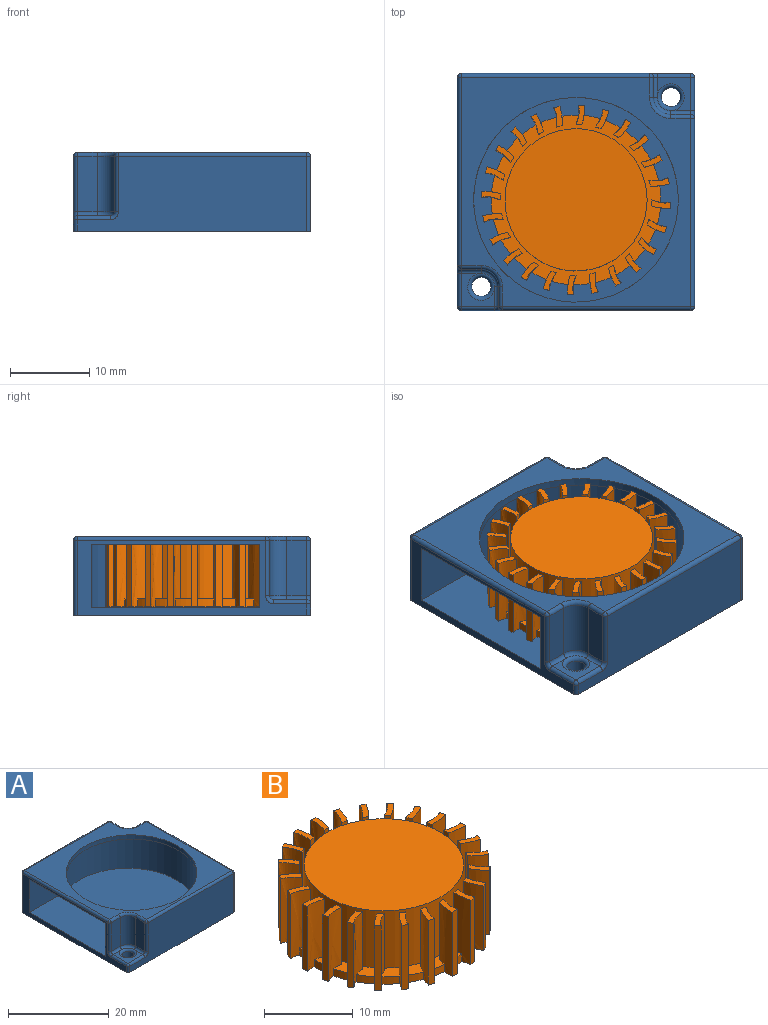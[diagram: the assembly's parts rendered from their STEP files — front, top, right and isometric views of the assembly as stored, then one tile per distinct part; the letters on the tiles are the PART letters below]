
ASSEMBLY  parts=2 mates=1
PART A: 64 faces, bbox 30x30x10 mm
  f0: plane 29x9.5mm, normal (-1,0,0), area 63.7mm2, adj f7,f21,f29,f32,f36,f45,f46,f58
  f1: plane 29x9.5mm, normal (0,1,0), area 234.1mm2, adj f7,f40,f46,f51,f54,f55,f57
  f2: plane 29x9.5mm, normal (1,0,0), area 234.1mm2, adj f7,f25,f33,f34,f37,f40,f41
  f3: plane 29x29mm, normal (0,0,1), area 263.2mm2, adj f26,f27,f31,f34,f35,f44,f45,f49
  f4: cylinder r=1.2mm len=2.4mm, axis (0,0,-1), area 11.3mm2, adj f7,f42
  f5: plane 29x9.5mm, normal (0,-1,0), area 234.1mm2, adj f7,f16,f17,f20,f21,f25,f26
  f6: cylinder r=1.2mm len=2.4mm, axis (0,0,-1), area 11.3mm2, adj f7,f19
  f7: plane 30x30mm, normal (0,0,-1), area 890.7mm2, adj f0,f1,f2,f4,f5,f6,f21,f25
  f8: plane 7x2.5mm, normal (-1,0,0), area 17.5mm2, adj f9,f17,f18,f27
  f9: cylinder r=2.2mm len=7mm, axis (0,0,1), area 24.2mm2, adj f8,f10,f23,f31
  f10: plane 7x2.5mm, normal (0,-1,0), area 17.5mm2, adj f9,f28,f35,f36
  f11: plane 4.2x4.2mm, normal (0,0,1), area 7.9mm2, adj f18,f19,f20,f28,f29
  f12: plane 7x2.5mm, normal (0,1,0), area 17.5mm2, adj f14,f33,f43,f44
  f13: plane 7x2.5mm, normal (1,0,0), area 17.5mm2, adj f14,f52,f53,f57
  f14: cylinder r=2.2mm len=7mm, axis (0,0,1), area 24.2mm2, adj f12,f13,f48,f49
  f15: plane 4.2x4.2mm, normal (0,0,1), area 7.9mm2, adj f41,f42,f43,f51,f52
  f16: torus R=1mm, axis (0,1,0), area 0.8mm2, adj f5,f17,f18,f20
  f17: cylinder r=0.5mm len=7mm, axis (0,0,-1), area 5.5mm2, adj f5,f8,f16,f22
  f18: cylinder r=0.5mm len=2.5mm, axis (0,1,0), area 2mm2, adj f8,f11,f16,f23
  f19: torus R=1.7mm, axis (0,0,1), area 6.8mm2, adj f6,f11,f23
  f20: cylinder r=0.5mm len=4.2mm, axis (-1,0,0), area 3.3mm2, adj f5,f11,f16,f24
  f21: cylinder r=0.5mm len=1.5mm, axis (0,0,-1), area 1.2mm2, adj f0,f5,f7,f24
  f22: sphere r=0.5mm, area 0.4mm2, adj f17,f26,f27
  f23: torus R=1.7mm, axis (0,0,1), area 2.5mm2, adj f9,f18,f19,f28
  f24: sphere r=0.5mm, area 0.4mm2, adj f20,f21,f29
  f25: cylinder r=0.5mm len=9.5mm, axis (0,0,1), area 7.5mm2, adj f2,f5,f7,f30
  f26: cylinder r=0.5mm len=23.8mm, axis (-1,0,0), area 18.7mm2, adj f3,f5,f22,f30
  f27: cylinder r=0.5mm len=2.5mm, axis (0,-1,0), area 2mm2, adj f3,f8,f22,f31
  f28: cylinder r=0.5mm len=2.5mm, axis (-1,0,0), area 2mm2, adj f10,f11,f23,f32
  f29: cylinder r=0.5mm len=4.2mm, axis (0,1,0), area 3.3mm2, adj f0,f11,f24,f32
  f30: sphere r=0.5mm, area 0.4mm2, adj f25,f26,f34
  f31: torus R=2.7mm, axis (0,0,1), area 2.9mm2, adj f3,f9,f27,f35
  f32: torus R=1mm, axis (1,0,0), area 0.8mm2, adj f0,f28,f29,f36
  f33: cylinder r=0.5mm len=7mm, axis (0,0,-1), area 5.5mm2, adj f2,f12,f37,f38
  f34: cylinder r=0.5mm len=23.8mm, axis (0,-1,0), area 18.7mm2, adj f2,f3,f30,f38
  f35: cylinder r=0.5mm len=2.5mm, axis (1,0,0), area 2mm2, adj f3,f10,f31,f39
  f36: cylinder r=0.5mm len=7mm, axis (0,0,-1), area 5.5mm2, adj f0,f10,f32,f39
  f37: torus R=1mm, axis (1,0,0), area 0.8mm2, adj f2,f33,f41,f43
  f38: sphere r=0.5mm, area 0.4mm2, adj f33,f34,f44
  f39: sphere r=0.5mm, area 0.4mm2, adj f35,f36,f45
  f40: cylinder r=0.5mm len=1.5mm, axis (0,0,-1), area 1.2mm2, adj f1,f2,f7,f47
  f41: cylinder r=0.5mm len=4.2mm, axis (0,-1,0), area 3.3mm2, adj f2,f15,f37,f47
  f42: torus R=1.7mm, axis (0,0,1), area 6.8mm2, adj f4,f15,f48
  f43: cylinder r=0.5mm len=2.5mm, axis (1,0,0), area 2mm2, adj f12,f15,f37,f48
  f44: cylinder r=0.5mm len=2.5mm, axis (-1,0,0), area 2mm2, adj f3,f12,f38,f49
  f45: cylinder r=0.5mm len=23.8mm, axis (0,1,0), area 18.7mm2, adj f0,f3,f39,f50
  f46: cylinder r=0.5mm len=9.5mm, axis (0,0,1), area 7.5mm2, adj f0,f1,f7,f50
  f47: sphere r=0.5mm, area 0.4mm2, adj f40,f41,f51
  f48: torus R=1.7mm, axis (0,0,1), area 2.5mm2, adj f14,f42,f43,f52
  f49: torus R=2.7mm, axis (0,0,1), area 2.9mm2, adj f3,f14,f44,f53
  f50: sphere r=0.5mm, area 0.4mm2, adj f45,f46,f54
  f51: cylinder r=0.5mm len=4.2mm, axis (1,0,0), area 3.3mm2, adj f1,f15,f47,f55
  f52: cylinder r=0.5mm len=2.5mm, axis (0,-1,0), area 2mm2, adj f13,f15,f48,f55
  f53: cylinder r=0.5mm len=2.5mm, axis (0,1,0), area 2mm2, adj f3,f13,f49,f56
  f54: cylinder r=0.5mm len=23.8mm, axis (1,0,0), area 18.7mm2, adj f1,f3,f50,f56
  f55: torus R=1mm, axis (0,1,0), area 0.8mm2, adj f1,f51,f52,f57
  f56: sphere r=0.5mm, area 0.4mm2, adj f53,f54,f57
  f57: cylinder r=0.5mm len=7mm, axis (0,0,-1), area 5.5mm2, adj f1,f13,f55,f56
  f58: plane 8x4.51mm, normal (0,1,0), area 36.1mm2, adj f0,f61,f62,f63
  f59: cylinder r=13.5mm len=21.27mm, axis (0,0,-1), area 273.3mm2, adj f60,f61,f62,f63
  f60: plane 10.42x8mm, normal (0,-1,0), area 83.4mm2, adj f0,f59,f61,f62
  f61: plane 28.5x22.1mm, normal (0,0,-1), area 124.5mm2, adj f0,f58,f59,f60,f63
  f62: plane 28.5x27.45mm, normal (0,0,1), area 651.4mm2, adj f0,f58,f59,f60,f63
  f63: cylinder r=12.95mm len=25.9mm, axis (0,0,1), area 284.8mm2, adj f3,f58,f59,f61,f62
PART B: 148 faces, bbox 23.9x23.9x8.9 mm
  f0: plane 18x18mm, normal (0,0,1), area 254.5mm2, adj f1
  f1: cylinder r=9mm len=18mm, axis (0,0,-1), area 446.7mm2, adj f0,f7
  f2: plane 2.41x1.11mm, normal (0,0,1), area 1.7mm2, adj f3,f4,f5,f6
  f3: plane 7.9x0.76mm, normal (0,-1,0), area 6mm2, adj f2,f4,f5,f7
  f4: extruded ~8.9x2.41mm, area 20.6mm2, adj f2,f3,f6,f7,f8,f147
  f5: extruded ~8.9x2.41mm, area 20.8mm2, adj f2,f3,f6,f7,f146,f147
  f6: plane 8.9x0.8mm, normal (0,1,0), area 7.1mm2, adj f2,f4,f5,f147
  f7: plane 21.52x21.52mm, normal (0,0,1), area 88.1mm2, adj f1,f3,f4,f5,f8,f10,f11,f12
  f8: cylinder r=10.75mm len=2.1mm, axis (0,0,-1), area 2.1mm2, adj f4,f7,f12,f147
  f9: plane 2.45x1.69mm, normal (0,0,1), area 1.7mm2, adj f10,f11,f12,f13
  f10: plane 7.9x0.73mm, normal (-0.26,-0.97,0), area 6mm2, adj f7,f9,f11,f12
  f11: extruded ~8.9x2.24mm, area 20.6mm2, adj f7,f9,f10,f13,f14,f147
  f12: extruded ~8.9x2.25mm, area 20.8mm2, adj f7,f8,f9,f10,f13,f147
  f13: plane 8.9x0.77mm, normal (0.26,0.97,0), area 7.1mm2, adj f9,f11,f12,f147
  f14: cylinder r=10.75mm len=1.93mm, axis (0,0,-1), area 2.1mm2, adj f7,f11,f18,f147
  f15: plane 2.32x2.17mm, normal (0,0,1), area 1.7mm2, adj f16,f17,f18,f19
  f16: plane 7.9x0.66mm, normal (-0.5,-0.87,0), area 6mm2, adj f7,f15,f17,f18
  f17: extruded ~8.9x1.92mm, area 20.6mm2, adj f7,f15,f16,f19,f20,f147
  f18: extruded ~8.9x1.94mm, area 20.8mm2, adj f7,f14,f15,f16,f19,f147
  f19: plane 8.9x0.69mm, normal (0.5,0.87,0), area 7.1mm2, adj f15,f17,f18,f147
  f20: cylinder r=10.75mm len=1.61mm, axis (0,0,-1), area 2.1mm2, adj f7,f17,f24,f147
  f21: plane 2.49x2.03mm, normal (0,0,1), area 1.7mm2, adj f22,f23,f24,f25
  f22: plane 7.9x0.54mm, normal (-0.71,-0.71,0), area 6mm2, adj f7,f21,f23,f24
  f23: extruded ~8.9x1.96mm, area 20.6mm2, adj f7,f21,f22,f25,f26,f147
  f24: extruded ~8.9x1.92mm, area 20.8mm2, adj f7,f20,f21,f22,f25,f147
  f25: plane 8.9x0.57mm, normal (0.71,0.71,0), area 7.1mm2, adj f21,f23,f24,f147
  f26: cylinder r=10.75mm len=1.78mm, axis (0,0,-1), area 2.1mm2, adj f7,f23,f30,f147
  f27: plane 2.64x1.6mm, normal (0,0,1), area 1.7mm2, adj f28,f29,f30,f31
  f28: plane 7.9x0.66mm, normal (-0.87,-0.5,0), area 6mm2, adj f7,f27,f29,f30
  f29: extruded ~8.9x2.27mm, area 20.6mm2, adj f7,f27,f28,f31,f32,f147
  f30: extruded ~8.9x2.24mm, area 20.8mm2, adj f7,f26,f27,f28,f31,f147
  f31: plane 8.9x0.69mm, normal (0.87,0.5,0), area 7.1mm2, adj f27,f29,f30,f147
  f32: cylinder r=10.75mm len=2.03mm, axis (0,0,-1), area 2.1mm2, adj f7,f29,f36,f147
  f33: plane 2.62x1.1mm, normal (0,0,1), area 1.7mm2, adj f34,f35,f36,f37
  f34: plane 7.9x0.73mm, normal (-0.97,-0.26,0), area 6mm2, adj f7,f33,f35,f36
  f35: extruded ~8.9x2.42mm, area 20.6mm2, adj f7,f33,f34,f37,f38,f147
  f36: extruded ~8.9x2.41mm, area 20.8mm2, adj f7,f32,f33,f34,f37,f147
  f37: plane 8.9x0.77mm, normal (0.97,0.26,0), area 7.1mm2, adj f33,f35,f36,f147
  f38: cylinder r=10.75mm len=2.14mm, axis (0,0,-1), area 2.1mm2, adj f7,f35,f42,f147
  f39: plane 2.41x1.11mm, normal (0,0,1), area 1.7mm2, adj f40,f41,f42,f43
  f40: plane 7.9x0.76mm, normal (-1,0,0), area 6mm2, adj f7,f39,f41,f42
  f41: extruded ~8.9x2.41mm, area 20.6mm2, adj f7,f39,f40,f43,f44,f147
  f42: extruded ~8.9x2.41mm, area 20.8mm2, adj f7,f38,f39,f40,f43,f147
  f43: plane 8.9x0.8mm, normal (1,0,0), area 7.1mm2, adj f39,f41,f42,f147
  f44: cylinder r=10.75mm len=2.1mm, axis (0,0,-1), area 2.1mm2, adj f7,f41,f48,f147
  f45: plane 2.45x1.69mm, normal (0,0,1), area 1.7mm2, adj f46,f47,f48,f49
  f46: plane 7.9x0.73mm, normal (-0.97,0.26,0), area 6mm2, adj f7,f45,f47,f48
  f47: extruded ~8.9x2.24mm, area 20.6mm2, adj f7,f45,f46,f49,f50,f147
  f48: extruded ~8.9x2.25mm, area 20.8mm2, adj f7,f44,f45,f46,f49,f147
  f49: plane 8.9x0.77mm, normal (0.97,-0.26,0), area 7.1mm2, adj f45,f47,f48,f147
  f50: cylinder r=10.75mm len=1.93mm, axis (0,0,-1), area 2.1mm2, adj f7,f47,f54,f147
  f51: plane 2.32x2.17mm, normal (0,0,1), area 1.7mm2, adj f52,f53,f54,f55
  f52: plane 7.9x0.66mm, normal (-0.87,0.5,0), area 6mm2, adj f7,f51,f53,f54
  f53: extruded ~8.9x1.92mm, area 20.6mm2, adj f7,f51,f52,f55,f56,f147
  f54: extruded ~8.9x1.94mm, area 20.8mm2, adj f7,f50,f51,f52,f55,f147
  f55: plane 8.9x0.69mm, normal (0.87,-0.5,0), area 7.1mm2, adj f51,f53,f54,f147
  f56: cylinder r=10.75mm len=1.61mm, axis (0,0,-1), area 2.1mm2, adj f7,f53,f60,f147
  f57: plane 2.49x2.03mm, normal (0,0,1), area 1.7mm2, adj f58,f59,f60,f61
  f58: plane 7.9x0.54mm, normal (-0.71,0.71,0), area 6mm2, adj f7,f57,f59,f60
  f59: extruded ~8.9x1.96mm, area 20.6mm2, adj f7,f57,f58,f61,f62,f147
  f60: extruded ~8.9x1.92mm, area 20.8mm2, adj f7,f56,f57,f58,f61,f147
  f61: plane 8.9x0.57mm, normal (0.71,-0.71,0), area 7.1mm2, adj f57,f59,f60,f147
  f62: cylinder r=10.75mm len=1.78mm, axis (0,0,-1), area 2.1mm2, adj f7,f59,f66,f147
  f63: plane 2.64x1.6mm, normal (0,0,1), area 1.7mm2, adj f64,f65,f66,f67
  f64: plane 7.9x0.66mm, normal (-0.5,0.87,0), area 6mm2, adj f7,f63,f65,f66
  f65: extruded ~8.9x2.27mm, area 20.6mm2, adj f7,f63,f64,f67,f68,f147
  f66: extruded ~8.9x2.24mm, area 20.8mm2, adj f7,f62,f63,f64,f67,f147
  f67: plane 8.9x0.69mm, normal (0.5,-0.87,0), area 7.1mm2, adj f63,f65,f66,f147
  f68: cylinder r=10.75mm len=2.03mm, axis (0,0,-1), area 2.1mm2, adj f7,f65,f72,f147
  f69: plane 2.62x1.1mm, normal (0,0,1), area 1.7mm2, adj f70,f71,f72,f73
  f70: plane 7.9x0.73mm, normal (-0.26,0.97,0), area 6mm2, adj f7,f69,f71,f72
  f71: extruded ~8.9x2.42mm, area 20.6mm2, adj f7,f69,f70,f73,f74,f147
  f72: extruded ~8.9x2.41mm, area 20.8mm2, adj f7,f68,f69,f70,f73,f147
  f73: plane 8.9x0.77mm, normal (0.26,-0.97,0), area 7.1mm2, adj f69,f71,f72,f147
  f74: cylinder r=10.75mm len=2.14mm, axis (0,0,-1), area 2.1mm2, adj f7,f71,f78,f147
  f75: plane 2.41x1.11mm, normal (0,0,1), area 1.7mm2, adj f76,f77,f78,f79
  f76: plane 7.9x0.76mm, normal (0,1,0), area 6mm2, adj f7,f75,f77,f78
  f77: extruded ~8.9x2.41mm, area 20.6mm2, adj f7,f75,f76,f79,f80,f147
  f78: extruded ~8.9x2.41mm, area 20.8mm2, adj f7,f74,f75,f76,f79,f147
  f79: plane 8.9x0.8mm, normal (0,-1,0), area 7.1mm2, adj f75,f77,f78,f147
  f80: cylinder r=10.75mm len=2.1mm, axis (0,0,-1), area 2.1mm2, adj f7,f77,f84,f147
  f81: plane 2.45x1.69mm, normal (0,0,1), area 1.7mm2, adj f82,f83,f84,f85
  f82: plane 7.9x0.73mm, normal (0.26,0.97,0), area 6mm2, adj f7,f81,f83,f84
  f83: extruded ~8.9x2.24mm, area 20.6mm2, adj f7,f81,f82,f85,f86,f147
  f84: extruded ~8.9x2.25mm, area 20.8mm2, adj f7,f80,f81,f82,f85,f147
  f85: plane 8.9x0.77mm, normal (-0.26,-0.97,0), area 7.1mm2, adj f81,f83,f84,f147
  f86: cylinder r=10.75mm len=1.93mm, axis (0,0,-1), area 2.1mm2, adj f7,f83,f90,f147
  f87: plane 2.32x2.17mm, normal (0,0,1), area 1.7mm2, adj f88,f89,f90,f91
  f88: plane 7.9x0.66mm, normal (0.5,0.87,0), area 6mm2, adj f7,f87,f89,f90
  f89: extruded ~8.9x1.92mm, area 20.6mm2, adj f7,f87,f88,f91,f92,f147
  f90: extruded ~8.9x1.94mm, area 20.8mm2, adj f7,f86,f87,f88,f91,f147
  f91: plane 8.9x0.69mm, normal (-0.5,-0.87,0), area 7.1mm2, adj f87,f89,f90,f147
  f92: cylinder r=10.75mm len=1.61mm, axis (0,0,-1), area 2.1mm2, adj f7,f89,f96,f147
  f93: plane 2.49x2.03mm, normal (0,0,1), area 1.7mm2, adj f94,f95,f96,f97
  f94: plane 7.9x0.54mm, normal (0.71,0.71,0), area 6mm2, adj f7,f93,f95,f96
  f95: extruded ~8.9x1.96mm, area 20.6mm2, adj f7,f93,f94,f97,f98,f147
  f96: extruded ~8.9x1.92mm, area 20.8mm2, adj f7,f92,f93,f94,f97,f147
  f97: plane 8.9x0.57mm, normal (-0.71,-0.71,0), area 7.1mm2, adj f93,f95,f96,f147
  f98: cylinder r=10.75mm len=1.78mm, axis (0,0,-1), area 2.1mm2, adj f7,f95,f102,f147
  f99: plane 2.64x1.6mm, normal (0,0,1), area 1.7mm2, adj f100,f101,f102,f103
  f100: plane 7.9x0.66mm, normal (0.87,0.5,0), area 6mm2, adj f7,f99,f101,f102
  f101: extruded ~8.9x2.27mm, area 20.6mm2, adj f7,f99,f100,f103,f104,f147
  f102: extruded ~8.9x2.24mm, area 20.8mm2, adj f7,f98,f99,f100,f103,f147
  f103: plane 8.9x0.69mm, normal (-0.87,-0.5,0), area 7.1mm2, adj f99,f101,f102,f147
  f104: cylinder r=10.75mm len=2.03mm, axis (0,0,-1), area 2.1mm2, adj f7,f101,f108,f147
  f105: plane 2.62x1.1mm, normal (0,0,1), area 1.7mm2, adj f106,f107,f108,f109
  f106: plane 7.9x0.73mm, normal (0.97,0.26,0), area 6mm2, adj f7,f105,f107,f108
  f107: extruded ~8.9x2.42mm, area 20.6mm2, adj f7,f105,f106,f109,f110,f147
  f108: extruded ~8.9x2.41mm, area 20.8mm2, adj f7,f104,f105,f106,f109,f147
  f109: plane 8.9x0.77mm, normal (-0.97,-0.26,0), area 7.1mm2, adj f105,f107,f108,f147
  f110: cylinder r=10.75mm len=2.14mm, axis (0,0,-1), area 2.1mm2, adj f7,f107,f114,f147
  f111: plane 2.41x1.11mm, normal (0,0,1), area 1.7mm2, adj f112,f113,f114,f115
  f112: plane 7.9x0.76mm, normal (1,0,0), area 6mm2, adj f7,f111,f113,f114
  f113: extruded ~8.9x2.41mm, area 20.6mm2, adj f7,f111,f112,f115,f116,f147
  f114: extruded ~8.9x2.41mm, area 20.8mm2, adj f7,f110,f111,f112,f115,f147
  f115: plane 8.9x0.8mm, normal (-1,0,0), area 7.1mm2, adj f111,f113,f114,f147
  f116: cylinder r=10.75mm len=2.1mm, axis (0,0,-1), area 2.1mm2, adj f7,f113,f120,f147
  f117: plane 2.45x1.69mm, normal (0,0,1), area 1.7mm2, adj f118,f119,f120,f121
  f118: plane 7.9x0.73mm, normal (0.97,-0.26,0), area 6mm2, adj f7,f117,f119,f120
  f119: extruded ~8.9x2.24mm, area 20.6mm2, adj f7,f117,f118,f121,f122,f147
  f120: extruded ~8.9x2.25mm, area 20.8mm2, adj f7,f116,f117,f118,f121,f147
  f121: plane 8.9x0.77mm, normal (-0.97,0.26,0), area 7.1mm2, adj f117,f119,f120,f147
  f122: cylinder r=10.75mm len=1.93mm, axis (0,0,-1), area 2.1mm2, adj f7,f119,f126,f147
  f123: plane 2.32x2.17mm, normal (0,0,1), area 1.7mm2, adj f124,f125,f126,f127
  f124: plane 7.9x0.66mm, normal (0.87,-0.5,0), area 6mm2, adj f7,f123,f125,f126
  f125: extruded ~8.9x1.92mm, area 20.6mm2, adj f7,f123,f124,f127,f128,f147
  f126: extruded ~8.9x1.94mm, area 20.8mm2, adj f7,f122,f123,f124,f127,f147
  f127: plane 8.9x0.69mm, normal (-0.87,0.5,0), area 7.1mm2, adj f123,f125,f126,f147
  f128: cylinder r=10.75mm len=1.61mm, axis (0,0,-1), area 2.1mm2, adj f7,f125,f132,f147
  f129: plane 2.49x2.03mm, normal (0,0,1), area 1.7mm2, adj f130,f131,f132,f133
  f130: plane 7.9x0.54mm, normal (0.71,-0.71,0), area 6mm2, adj f7,f129,f131,f132
  f131: extruded ~8.9x1.96mm, area 20.6mm2, adj f7,f129,f130,f133,f134,f147
  f132: extruded ~8.9x1.92mm, area 20.8mm2, adj f7,f128,f129,f130,f133,f147
  f133: plane 8.9x0.57mm, normal (-0.71,0.71,0), area 7.1mm2, adj f129,f131,f132,f147
  f134: cylinder r=10.75mm len=1.78mm, axis (0,0,-1), area 2.1mm2, adj f7,f131,f136,f147
  f135: extruded ~8.9x2.27mm, area 20.6mm2, adj f7,f137,f138,f139,f140,f147
  f136: extruded ~8.9x2.24mm, area 20.8mm2, adj f7,f134,f137,f138,f139,f147
  f137: plane 2.64x1.6mm, normal (0,0,1), area 1.7mm2, adj f135,f136,f138,f139
  f138: plane 7.9x0.66mm, normal (0.5,-0.87,0), area 6mm2, adj f7,f135,f136,f137
  f139: plane 8.9x0.69mm, normal (-0.5,0.87,0), area 7.1mm2, adj f135,f136,f137,f147
  f140: cylinder r=10.75mm len=2.03mm, axis (0,0,-1), area 2.1mm2, adj f7,f135,f142,f147
  f141: extruded ~8.9x2.42mm, area 20.6mm2, adj f7,f143,f144,f145,f146,f147
  f142: extruded ~8.9x2.41mm, area 20.8mm2, adj f7,f140,f143,f144,f145,f147
  f143: plane 2.62x1.1mm, normal (0,0,1), area 1.7mm2, adj f141,f142,f144,f145
  f144: plane 7.9x0.73mm, normal (0.26,-0.97,0), area 6mm2, adj f7,f141,f142,f143
  f145: plane 8.9x0.77mm, normal (-0.26,0.97,0), area 7.1mm2, adj f141,f142,f143,f147
  f146: cylinder r=10.75mm len=2.14mm, axis (0,0,-1), area 2.1mm2, adj f5,f7,f141,f147
  f147: plane 23.9x23.9mm, normal (0,0,-1), area 383.3mm2, adj f4,f5,f6,f8,f11,f12,f13,f14
PLACE A at identity
PLACE B at identity
MATE revolute B.f1 <-> A.f63  axis (0,0,1) through (0,-1,10)mm
